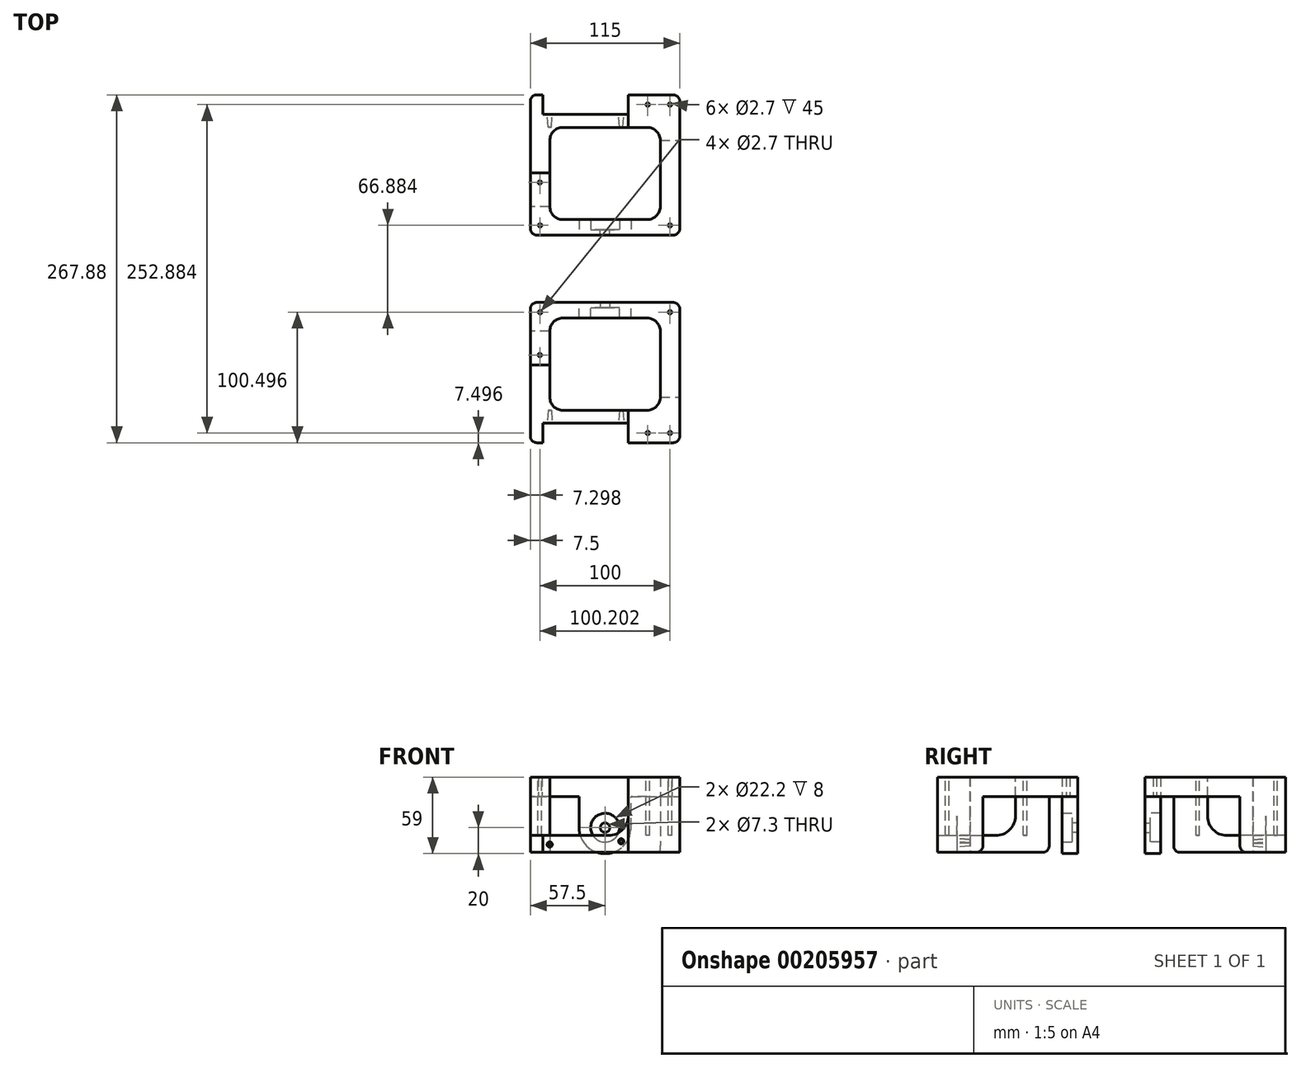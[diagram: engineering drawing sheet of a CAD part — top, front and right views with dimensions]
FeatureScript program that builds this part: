
annotation { "Feature Type Name" : "Feature", "Feature Type Description" : "" }
export const myFeature = defineFeature(function(context is Context, id is Id, definition is map)
    precondition{}
    {
        {
            var Q0;
            Q0=qCreatedBy(makeId("Top.planeOp"),FACE);
            var sketch = newSketch(context, id + "F0", { "sketchPlane" : qUnion([Q0])});
            skPoint(sketch, "E0.middle", {"position": v(0, 0) * mm});
            skLineSegment(sketch, "E1.bottom", {"start": v(32.5, 60.5) * mm, "end": v(-32.5, 60.5) * mm});
            skArc(sketch, "E2.filletArc", {"start": v(-32.5, 60.5) * mm, "mid": v(-39.57, 57.57) * mm, "end": v(-42.5, 50.5) * mm});
            skArc(sketch, "E3.filletArc", {"start": v(42.5, 50.5) * mm, "mid": v(39.57, 57.57) * mm, "end": v(32.5, 60.5) * mm});
            skLineSegment(sketch, "E4", {"start": v(0, 97.59) * mm, "end": v(0, -46.14) * mm, "construction": true});
            skPoint(sketch, "E4.endSnap0", {"position": v(0, 60.5) * mm});
            skLineSegment(sketch, "E5", {"start": v(-47.9, 85.5) * mm, "end": v(-47.9, 70.5) * mm});
            skLineSegment(sketch, "E6", {"start": v(17.9, 85.5) * mm, "end": v(17.9, 70.5) * mm});
            skLineSegment(sketch, "E7", {"start": v(17.9, 70.5) * mm, "end": v(-47.9, 70.5) * mm});
            skLineSegment(sketch, "E8", {"start": v(-47.9, 85.5) * mm, "end": v(-52.5, 85.5) * mm});
            skLineSegment(sketch, "E9", {"start": v(-42.5, 50.5) * mm, "end": v(-42.5, -0.5) * mm});
            skPoint(sketch, "E10.visualSharp", {"position": v(-57.5, 85.5) * mm});
            skArc(sketch, "E10.filletArc", {"start": v(-52.5, 85.5) * mm, "mid": v(-56.04, 84.04) * mm, "end": v(-57.5, 80.5) * mm});
            skLineSegment(sketch, "E11", {"start": v(-57.5, 80.5) * mm, "end": v(-57.5, -0.5) * mm});
            skLineSegment(sketch, "E12", {"start": v(17.9, 85.5) * mm, "end": v(52.5, 85.5) * mm});
            skLineSegment(sketch, "E13", {"start": v(57.5, 80.5) * mm, "end": v(57.5, 50.5) * mm});
            skPoint(sketch, "E14.visualSharp", {"position": v(57.5, 85.5) * mm});
            skArc(sketch, "E14.filletArc", {"start": v(57.5, 80.5) * mm, "mid": v(56.04, 84.04) * mm, "end": v(52.5, 85.5) * mm});
            skLineSegment(sketch, "E15", {"start": v(42.5, 50.5) * mm, "end": v(57.5, 50.5) * mm});
            skLineSegment(sketch, "E16", {"start": v(-57.5, -0.5) * mm, "end": v(-42.5, -0.5) * mm});
            skLineSegment(sketch, "E17", {"start": v(-97.59, -48.44) * mm, "end": v(103.09, -48.44) * mm, "construction": true});
            skSolve(sketch);
        }
        {
            var Q0;
            Q0=qSketchRegion(id+"F0",true);
            extrude(context, id + "F1", {"entities" : qUnion([Q0]), "depth" : 13 * mm});
        }
        {
            var Q0;
            Q0=qCreatedBy(makeId("Top.planeOp"),FACE);
            cPlane(context, id + "F2", {"entities" : qUnion([Q0]), "cplaneType" : CPlaneType.OFFSET, "offset" : 43 * mm, "width" : 150 * mm, "height" : 150 * mm});
        }
        {
            var Q0;
            Q0=qCreatedBy(id+"F2.planeOp",FACE);
            var sketch = newSketch(context, id + "F3", { "sketchPlane" : qUnion([Q0])});
            skPoint(sketch, "E18.middle", {"position": v(-8.03, -3.4) * mm});
            skPoint(sketch, "E19.middle", {"position": v(-8.03, 0) * mm});
            skLineSegment(sketch, "E20", {"start": v(0, 97.59) * mm, "end": v(0, -46.14) * mm, "construction": true});
            skPoint(sketch, "E20.endSnap0", {"position": v(0, 60.5) * mm});
            skLineSegment(sketch, "E21", {"start": v(32.5, -10.5) * mm, "end": v(-32.5, -10.5) * mm});
            skPoint(sketch, "E22.visualSharp", {"position": v(42.5, -10.5) * mm});
            skArc(sketch, "E22.filletArc", {"start": v(32.5, -10.5) * mm, "mid": v(39.57, -7.57) * mm, "end": v(42.5, -0.5) * mm});
            skPoint(sketch, "E23.visualSharp", {"position": v(-42.5, -10.5) * mm});
            skArc(sketch, "E23.filletArc", {"start": v(-42.5, -0.5) * mm, "mid": v(-39.57, -7.57) * mm, "end": v(-32.5, -10.5) * mm});
            skLineSegment(sketch, "E24", {"start": v(-57.5, 25.5) * mm, "end": v(-57.5, -17.5) * mm});
            skLineSegment(sketch, "E25", {"start": v(17.9, 85.5) * mm, "end": v(52.5, 85.5) * mm});
            skLineSegment(sketch, "E26", {"start": v(57.5, 80.5) * mm, "end": v(57.5, -17.5) * mm});
            skPoint(sketch, "E27.visualSharp", {"position": v(57.5, 85.5) * mm});
            skArc(sketch, "E27.filletArc", {"start": v(57.5, 80.5) * mm, "mid": v(56.04, 84.04) * mm, "end": v(52.5, 85.5) * mm});
            skLineSegment(sketch, "E28", {"start": v(-42.5, -0.5) * mm, "end": v(-42.5, 25.5) * mm});
            skLineSegment(sketch, "E29", {"start": v(42.5, -0.5) * mm, "end": v(42.5, 50.5) * mm});
            skPoint(sketch, "E30.visualSharp", {"position": v(42.5, 60.5) * mm});
            skArc(sketch, "E30.filletArc", {"start": v(42.5, 50.5) * mm, "mid": v(39.57, 57.57) * mm, "end": v(32.5, 60.5) * mm});
            skLineSegment(sketch, "E31", {"start": v(-52.5, -22.5) * mm, "end": v(52.5, -22.5) * mm});
            skArc(sketch, "E32.filletArc", {"start": v(-57.5, -17.5) * mm, "mid": v(-56.04, -21.04) * mm, "end": v(-52.5, -22.5) * mm});
            skArc(sketch, "E33.filletArc", {"start": v(52.5, -22.5) * mm, "mid": v(56.04, -21.04) * mm, "end": v(57.5, -17.5) * mm});
            skLineSegment(sketch, "E34", {"start": v(17.9, 60.5) * mm, "end": v(17.9, 85.5) * mm});
            skPoint(sketch, "E35.start.orphan", {"position": v(17.9, 70.5) * mm});
            skLineSegment(sketch, "E36.trimOffspring", {"start": v(17.9, 60.5) * mm, "end": v(32.5, 60.5) * mm});
            skLineSegment(sketch, "E37", {"start": v(-52.43, 25.5) * mm, "end": v(7.9, 25.5) * mm});
            skLineSegment(sketch, "E38", {"start": v(17.9, 60.5) * mm, "end": v(17.9, 35.5) * mm});
            skPoint(sketch, "E39.visualSharp", {"position": v(17.9, 25.5) * mm});
            skArc(sketch, "E39.filletArc", {"start": v(7.9, 25.5) * mm, "mid": v(14.97, 28.43) * mm, "end": v(17.9, 35.5) * mm});
            skLineSegment(sketch, "E40", {"start": v(-52.43, 25.5) * mm, "end": v(-57.5, 25.5) * mm});
            skLineSegment(sketch, "E41", {"start": v(42.5, 50.5) * mm, "end": v(57.5, 50.5) * mm});
            skLineSegment(sketch, "E42", {"start": v(-42.5, -0.5) * mm, "end": v(-57.5, -0.5) * mm});
            skCircle(sketch, "E43", {"center": v(-50.2, 18) * mm, "radius": 1.35 * mm});
            skCircle(sketch, "E44", {"center": v(-50, -15) * mm, "radius": 1.35 * mm});
            skCircle(sketch, "E45", {"center": v(50, -15) * mm, "radius": 1.35 * mm});
            skCircle(sketch, "E46", {"center": v(50, 78) * mm, "radius": 1.35 * mm});
            skCircle(sketch, "E47", {"center": v(17, 18) * mm, "radius": 1.35 * mm});
            skCircle(sketch, "E48", {"center": v(32.9, 78) * mm, "radius": 1.35 * mm});
            skLineSegment(sketch, "E49", {"start": v(50, -15) * mm, "end": v(-16.38, 51.38) * mm, "construction": true});
            skSolve(sketch);
        }
        {
            var Q0;
            {var subQ1=sQuery(id+"F3.wireOp",EDGE,"E28");Q0=makeQuery(id+"F3.imprint","IMPRINT",FACE,{"disambiguationData":[TD([[makeQuery(id+"F3.imprint","IMPRINT",EDGE,{"derivedFrom":subQ1}),1.0]])]});}
            var Q1;
            Q1=makeQuery(id+"F3.imprint","IMPRINT",FACE,{"disambiguationData":[TD([[makeQuery(id+"F3.imprint","IMPRINT",EDGE,{"derivedFrom":sQuery(id+"F3.wireOp",EDGE,"E25")}),-1.0]])]});
            extrude(context, id + "F4", {"entities" : qUnion([Q0, Q1]), "operationType" : NewBodyOperationType.ADD, "oppositeDirection" : true, "depth" : 43 * mm});
        }
        {
            var Q0;
            Q0=makeQuery(id+"F3.imprint","IMPRINT",FACE,{"disambiguationData":[TD([[makeQuery(id+"F3.imprint","IMPRINT",EDGE,{"derivedFrom":sQuery(id+"F3.wireOp",EDGE,"E21")}),1.0]])]});
            var Q1;
            {var subQ2=sQuery(id+"F3.wireOp",EDGE,"E28");Q1=makeQuery(id+"F3.imprint","IMPRINT",FACE,{"disambiguationData":[TD([[makeQuery(id+"F3.imprint","IMPRINT",EDGE,{"derivedFrom":subQ2}),1.0]])]});}
            var Q2;
            Q2=makeQuery(id+"F3.imprint","IMPRINT",FACE,{"disambiguationData":[TD([[makeQuery(id+"F3.imprint","IMPRINT",EDGE,{"derivedFrom":sQuery(id+"F3.wireOp",EDGE,"E25")}),-1.0]])]});
            extrude(context, id + "F5", {"entities" : qUnion([Q0, Q1, Q2]), "operationType" : NewBodyOperationType.ADD, "depth" : 15 * mm});
        }
        {
            var Q0;
            Q0=makeQuery(id+"F5.opExtrude","SWEPT_FACE",FACE,{"disambiguationData":[OSD([sQuery(id+"F3.wireOp",EDGE,"E31")])]});
            cPlane(context, id + "F6", {"entities" : qUnion([Q0]), "cplaneType" : CPlaneType.OFFSET, "offset" : 4 * mm, "oppositeDirection" : true, "width" : 150 * mm, "height" : 150 * mm});
        }
        {
            var Q0;
            Q0=qCreatedBy(id+"F6.planeOp",FACE);
            var sketch = newSketch(context, id + "F7", { "sketchPlane" : qUnion([Q0])});
            skCircle(sketch, "E50", {"center": v(0, 19) * mm, "radius": 11.1 * mm});
            skLineSegment(sketch, "E51", {"start": v(-20, 43) * mm, "end": v(20, 43) * mm});
            skLineSegment(sketch, "E52", {"start": v(-20, 19) * mm, "end": v(-20, 43) * mm});
            skLineSegment(sketch, "E53", {"start": v(20, 19) * mm, "end": v(20, 43) * mm});
            skArc(sketch, "E54", {"start": v(-20, 19) * mm, "mid": v(0, -1) * mm, "end": v(20, 19) * mm});
            skCircle(sketch, "E55", {"center": v(0, 19) * mm, "radius": 3.65 * mm});
            skSolve(sketch);
        }
        {
            var Q0;
            Q0=makeQuery(id+"F7.imprint","IMPRINT",FACE,{"disambiguationData":[TD([[makeQuery(id+"F7.imprint","IMPRINT",EDGE,{"derivedFrom":sQuery(id+"F7.wireOp",EDGE,"E50")}),-1.0]])]});
            extrude(context, id + "F8", {"entities" : qUnion([Q0]), "operationType" : NewBodyOperationType.ADD, "oppositeDirection" : true, "depth" : 8 * mm});
        }
        {
            var Q0;
            Q0=makeQuery(id+"F7.imprint","IMPRINT",FACE,{"disambiguationData":[TD([[makeQuery(id+"F7.imprint","IMPRINT",EDGE,{"derivedFrom":sQuery(id+"F7.wireOp",EDGE,"E50")}),1.0]])]});
            extrude(context, id + "F9", {"entities" : qUnion([Q0]), "operationType" : NewBodyOperationType.REMOVE, "oppositeDirection" : true, "depth" : 25 * mm});
        }
        {
            var Q0;
            Q0=makeQuery(id+"F7.imprint","IMPRINT",FACE,{"disambiguationData":[TD([[makeQuery(id+"F7.imprint","IMPRINT",EDGE,{"derivedFrom":sQuery(id+"F7.wireOp",EDGE,"E50")}),-1.0]])]});
            var Q1;
            Q1=makeQuery(id+"F7.imprint","IMPRINT",FACE,{"disambiguationData":[TD([[makeQuery(id+"F7.imprint","IMPRINT",EDGE,{"derivedFrom":sQuery(id+"F7.wireOp",EDGE,"E50")}),1.0]])]});
            extrude(context, id + "F10", {"entities" : qUnion([Q0, Q1]), "operationType" : NewBodyOperationType.ADD, "depth" : 4 * mm});
        }
        {
            var Q0;
            Q0=makeQuery(id+"F1.opExtrude","SWEPT_FACE",FACE,{"disambiguationData":[OSD([sQuery(id+"F0.wireOp",EDGE,"E7")])]});
            cPlane(context, id + "F11", {"entities" : qUnion([Q0]), "cplaneType" : CPlaneType.OFFSET, "offset" : 0 * mm, "width" : 150 * mm, "height" : 150 * mm});
        }
        {
            var Q0;
            Q0=qCreatedBy(id+"F11.planeOp",FACE);
            var sketch = newSketch(context, id + "F12", { "sketchPlane" : qUnion([Q0])});
            skCircle(sketch, "E56", {"center": v(42.6, 6) * mm, "radius": 2 * mm});
            skCircle(sketch, "E57", {"center": v(-12.4, 8.5) * mm, "radius": 2 * mm});
            skSolve(sketch);
        }
        {
            var Q0;
            Q0=makeQuery(id+"F12.imprint","IMPRINT",FACE,{"disambiguationData":[TD([[makeQuery(id+"F12.imprint","IMPRINT",EDGE,{"derivedFrom":sQuery(id+"F12.wireOp",EDGE,"E57")}),1.0]])]});
            var Q1;
            Q1=makeQuery(id+"F12.imprint","IMPRINT",FACE,{"disambiguationData":[TD([[makeQuery(id+"F12.imprint","IMPRINT",EDGE,{"derivedFrom":sQuery(id+"F12.wireOp",EDGE,"E56")}),1.0]])]});
            extrude(context, id + "F13", {"entities" : qUnion([Q0, Q1]), "operationType" : NewBodyOperationType.REMOVE, "oppositeDirection" : true, "depth" : 9.8 * mm, "hasDraft" : true, "draftAngle" : 4 * degree, "draftPullDirection" : true});
        }
        {
            var Q0;
            Q0=makeQuery(id+"F1.opExtrude","CAP_EDGE",EDGE,{"disambiguationData":[OSD([sQuery(id+"F0.wireOp",EDGE,"E15")])],"isStart":true});
            var Q1;
            Q1=makeQuery(id+"F1.opExtrude","CAP_EDGE",EDGE,{"disambiguationData":[OSD([sQuery(id+"F0.wireOp",EDGE,"E16")])],"isStart":true});
            fillet(context, id + "F14", {"entities" : qUnion([Q0, Q1]), "radius" : 5 * mm, "tangentPropagation" : true, "allowEdgeOverflow" : false});
        }
        {
            var Q0;
            Q0=makeQuery(id+"F3.imprint","IMPRINT",FACE,{"disambiguationData":[TD([[makeQuery(id+"F3.imprint","IMPRINT",EDGE,{"derivedFrom":sQuery(id+"F3.wireOp",EDGE,"E21")}),-1.0]])]});
            extrude(context, id + "F15", {"entities" : qUnion([Q0]), "operationType" : NewBodyOperationType.REMOVE, "oppositeDirection" : true, "depth" : 15 * mm});
        }
        {
            var Q0;
            Q0=makeQuery(id+"F5.opExtrude","CAP_EDGE",EDGE,{"disambiguationData":[OSD([sQuery(id+"F3.wireOp",EDGE,"E42")])],"isStart":false});
            var Q1;
            Q1=makeQuery(id+"F5.opExtrude","CAP_EDGE",EDGE,{"disambiguationData":[OSD([sQuery(id+"F3.wireOp",EDGE,"E41")])],"isStart":false});
            var Q2;
            Q2=makeQuery(id+"F4.boolean.opBoolean","INTERSECT",EDGE,{"derivedFrom":[makeQuery(id+"F1.opExtrude","CAP_FACE",FACE,{"disambiguationData":[OSD([sQuery(id+"F0.wireOp",EDGE,"E1.bottom"),sQuery(id+"F0.wireOp",EDGE,"E2.filletArc"),sQuery(id+"F0.wireOp",EDGE,"E3.filletArc"),sQuery(id+"F0.wireOp",EDGE,"E5"),sQuery(id+"F0.wireOp",EDGE,"E6"),sQuery(id+"F0.wireOp",EDGE,"E7"),sQuery(id+"F0.wireOp",EDGE,"E8"),sQuery(id+"F0.wireOp",EDGE,"E9"),sQuery(id+"F0.wireOp",EDGE,"E10.filletArc"),sQuery(id+"F0.wireOp",EDGE,"E11"),sQuery(id+"F0.wireOp",EDGE,"E12"),sQuery(id+"F0.wireOp",EDGE,"E13"),sQuery(id+"F0.wireOp",EDGE,"E14.filletArc"),sQuery(id+"F0.wireOp",EDGE,"E15"),sQuery(id+"F0.wireOp",EDGE,"E16")])],"isStart":false}),makeQuery(id+"F4.opExtrude","SWEPT_FACE",FACE,{"disambiguationData":[OSD([sQuery(id+"F3.wireOp",EDGE,"E34")])]})]});
            var Q3;
            Q3=makeQuery(id+"F4.boolean.opBoolean","INTERSECT",EDGE,{"derivedFrom":[makeQuery(id+"F1.opExtrude","CAP_FACE",FACE,{"disambiguationData":[OSD([sQuery(id+"F0.wireOp",EDGE,"E1.bottom"),sQuery(id+"F0.wireOp",EDGE,"E2.filletArc"),sQuery(id+"F0.wireOp",EDGE,"E3.filletArc"),sQuery(id+"F0.wireOp",EDGE,"E5"),sQuery(id+"F0.wireOp",EDGE,"E6"),sQuery(id+"F0.wireOp",EDGE,"E7"),sQuery(id+"F0.wireOp",EDGE,"E8"),sQuery(id+"F0.wireOp",EDGE,"E9"),sQuery(id+"F0.wireOp",EDGE,"E10.filletArc"),sQuery(id+"F0.wireOp",EDGE,"E11"),sQuery(id+"F0.wireOp",EDGE,"E12"),sQuery(id+"F0.wireOp",EDGE,"E13"),sQuery(id+"F0.wireOp",EDGE,"E14.filletArc"),sQuery(id+"F0.wireOp",EDGE,"E15"),sQuery(id+"F0.wireOp",EDGE,"E16")])],"isStart":false}),makeQuery(id+"F4.opExtrude","SWEPT_FACE",FACE,{"disambiguationData":[OSD([sQuery(id+"F3.wireOp",EDGE,"E37"),sQuery(id+"F3.wireOp",EDGE,"E40")])]})]});
            var Q4;
            Q4=makeQuery(id+"F4.opExtrude","CAP_EDGE",EDGE,{"disambiguationData":[OSD([sQuery(id+"F3.wireOp",EDGE,"E42")])],"isStart":true});
            var Q5;
            Q5=makeQuery(id+"F4.opExtrude","CAP_EDGE",EDGE,{"disambiguationData":[OSD([sQuery(id+"F3.wireOp",EDGE,"E41")])],"isStart":true});
            fillet(context, id + "F16", {"entities" : qUnion([Q0, Q1, Q2, Q3, Q4, Q5]), "radius" : 15 * mm, "tangentPropagation" : true, "allowEdgeOverflow" : false});
        }
        {
            var Q0;
            Q0=sQuery(id+"F0.wireOp",EDGE,"E17");
            cPlane(context, id + "F17", {"entities" : qUnion([Q0]), "cplaneType" : CPlaneType.LINE_ANGLE, "offset" : 25 * mm, "angle" : 0 * degree, "width" : 150 * mm, "height" : 150 * mm});
        }
        {
            var Q0;
            Q0=makeQuery(id+"F1.opExtrude","SWEPT_BODY",BODY,{"disambiguationData":[OSD([sQuery(id+"F0.wireOp",EDGE,"E1.bottom"),sQuery(id+"F0.wireOp",EDGE,"E2.filletArc"),sQuery(id+"F0.wireOp",EDGE,"E3.filletArc"),sQuery(id+"F0.wireOp",EDGE,"E5"),sQuery(id+"F0.wireOp",EDGE,"E6"),sQuery(id+"F0.wireOp",EDGE,"E7"),sQuery(id+"F0.wireOp",EDGE,"E8"),sQuery(id+"F0.wireOp",EDGE,"E9"),sQuery(id+"F0.wireOp",EDGE,"E10.filletArc"),sQuery(id+"F0.wireOp",EDGE,"E11"),sQuery(id+"F0.wireOp",EDGE,"E12"),sQuery(id+"F0.wireOp",EDGE,"E13"),sQuery(id+"F0.wireOp",EDGE,"E14.filletArc"),sQuery(id+"F0.wireOp",EDGE,"E15"),sQuery(id+"F0.wireOp",EDGE,"E16")])]});
            var Q1;
            Q1=qCreatedBy(id+"F17.planeOp",FACE);
            mirror(context, id + "F18", {"entities" : qUnion([Q0]), "mirrorPlane" : qUnion([Q1])});
        }
    });
